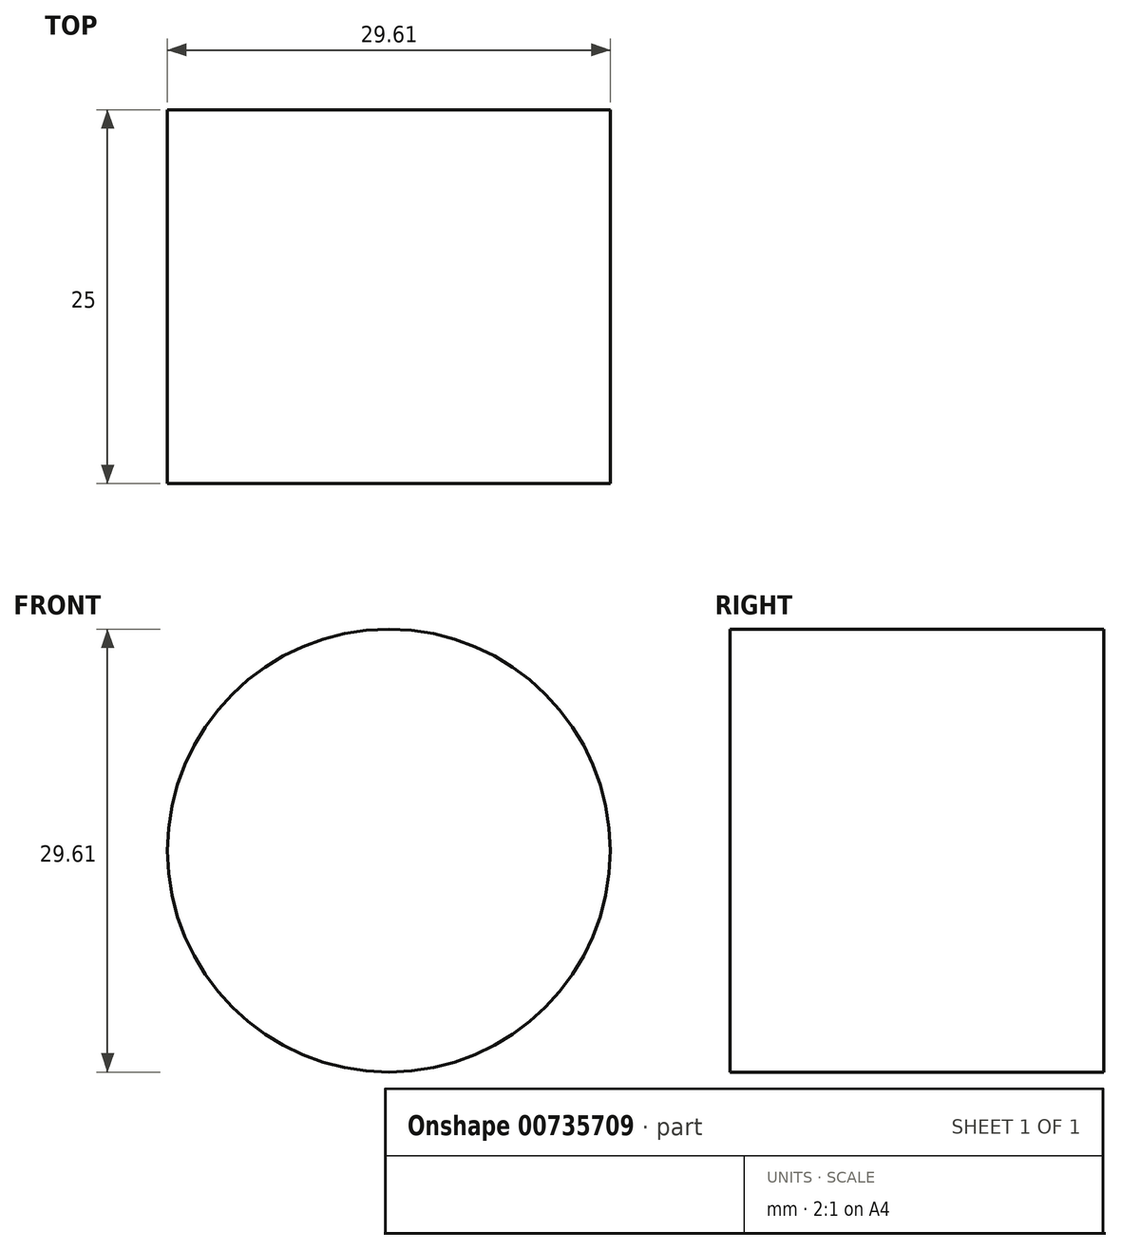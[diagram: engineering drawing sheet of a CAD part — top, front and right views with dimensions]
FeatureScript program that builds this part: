
annotation { "Feature Type Name" : "Feature", "Feature Type Description" : "" }
export const myFeature = defineFeature(function(context is Context, id is Id, definition is map)
    precondition{}
    {
        {
            var Q0;
            Q0=qCreatedBy(makeId("Front.planeOp"),FACE);
            var sketch = newSketch(context, id + "F0", { "sketchPlane" : qUnion([Q0])});
            skCircle(sketch, "E0", {"center": v(-19.63, 13) * mm, "radius": 14.8 * mm});
            skSolve(sketch);
        }
        {
            var Q0;
            Q0=makeQuery(id+"F0.imprint","IMPRINT",FACE,{"disambiguationData":[TD([[makeQuery(id+"F0.imprint","IMPRINT",EDGE,{"derivedFrom":sQuery(id+"F0.wireOp",EDGE,"E0")}),1.0]])]});
            extrude(context, id + "F1", {"entities" : qUnion([Q0]), "depth" : 25 * mm, "offsetDistance" : 25 * mm});
        }
    });
